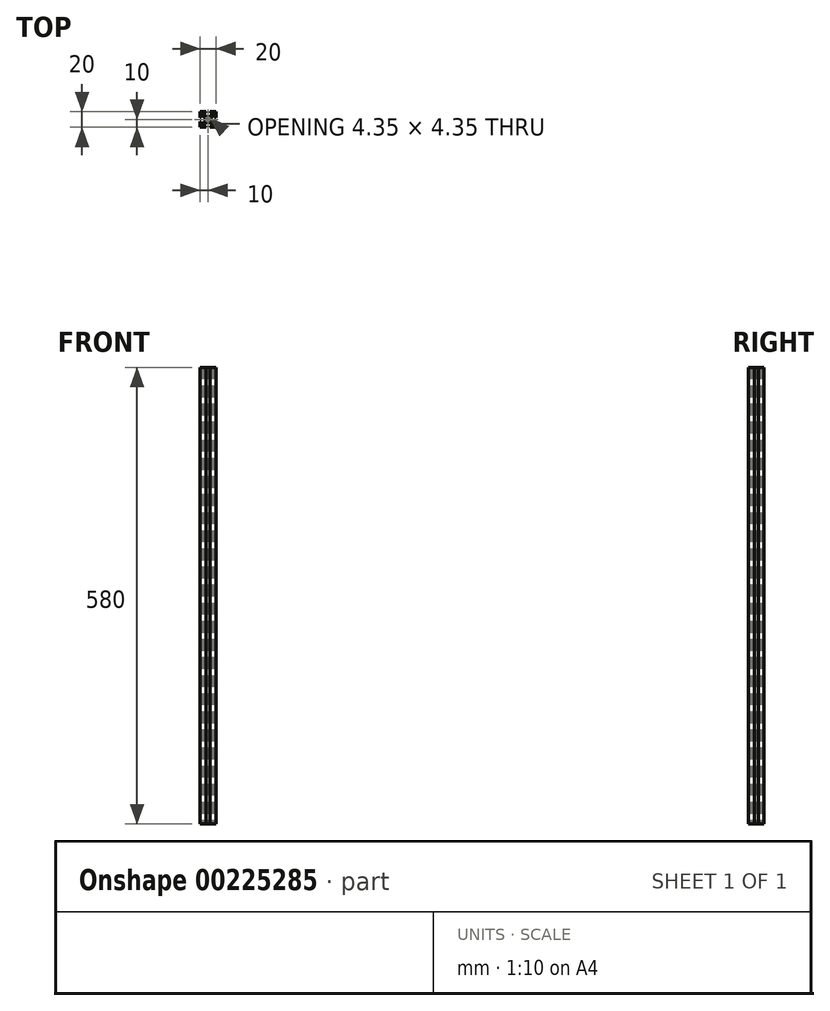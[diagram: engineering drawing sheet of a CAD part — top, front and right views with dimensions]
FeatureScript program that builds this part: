
annotation { "Feature Type Name" : "Feature", "Feature Type Description" : "" }
export const myFeature = defineFeature(function(context is Context, id is Id, definition is map)
    precondition{}
    {
        {
            var Q0;
            Q0=qCreatedBy(makeId("Top.planeOp"),FACE);
            var sketch = newSketch(context, id + "F0", { "sketchPlane" : qUnion([Q0])});
            skLineSegment(sketch, "E0.bottom", {"start": v(10, 10) * mm, "end": v(-10, 10) * mm});
            skLineSegment(sketch, "E0.top", {"start": v(10, -10) * mm, "end": v(-10, -10) * mm});
            skLineSegment(sketch, "E0.left", {"start": v(10, 10) * mm, "end": v(10, -10) * mm});
            skLineSegment(sketch, "E0.right", {"start": v(-10, 10) * mm, "end": v(-10, -10) * mm});
            skPoint(sketch, "E0.middle", {"position": v(0, 0) * mm});
            skLineSegment(sketch, "E1", {"start": v(-10, 10) * mm, "end": v(10, -10) * mm, "construction": true});
            skLineSegment(sketch, "E2", {"start": v(-10, -10) * mm, "end": v(10, 10) * mm, "construction": true});
            skLineSegment(sketch, "E3", {"start": v(0, 10) * mm, "end": v(0, -10) * mm, "construction": true});
            skLineSegment(sketch, "E4", {"start": v(-10, 0) * mm, "end": v(10, 0) * mm, "construction": true});
            skPoint(sketch, "E4.endSnap0", {"position": v(10, 0) * mm});
            skLineSegment(sketch, "E5", {"start": v(-2.63, 13.49) * mm, "end": v(2.63, 13.49) * mm});
            skLineSegment(sketch, "E6", {"start": v(2.63, 13.49) * mm, "end": v(2.63, 8.5) * mm});
            skLineSegment(sketch, "E7", {"start": v(2.63, 8.5) * mm, "end": v(6, 8.5) * mm});
            skLineSegment(sketch, "E8", {"start": v(6, 8.5) * mm, "end": v(6, 7.06) * mm});
            skLineSegment(sketch, "E9", {"start": v(6, 7.06) * mm, "end": v(2.6, 3.66) * mm});
            skLineSegment(sketch, "E10", {"start": v(2.6, 3.66) * mm, "end": v(-2.6, 3.66) * mm});
            skLineSegment(sketch, "E11", {"start": v(-2.6, 3.66) * mm, "end": v(-6, 7.06) * mm});
            skLineSegment(sketch, "E12", {"start": v(-6, 7.06) * mm, "end": v(-6, 8.5) * mm});
            skLineSegment(sketch, "E13", {"start": v(-6, 8.5) * mm, "end": v(-2.63, 8.5) * mm});
            skLineSegment(sketch, "E14", {"start": v(-2.63, 8.5) * mm, "end": v(-2.63, 13.49) * mm});
            skCircle(sketch, "E15", {"center": v(0, 0) * mm, "radius": 2.1 * mm});
            skLineSegment(sketch, "E16.MirrorCS", {"start": v(-7.06, 6) * mm, "end": v(-8.5, 6) * mm});
            skLineSegment(sketch, "E17.MirrorCS", {"start": v(-3.66, 2.6) * mm, "end": v(-7.06, 6) * mm});
            skLineSegment(sketch, "E18.MirrorCS", {"start": v(-8.5, 6) * mm, "end": v(-8.5, 2.63) * mm});
            skLineSegment(sketch, "E19.MirrorCS", {"start": v(-3.66, -2.6) * mm, "end": v(-3.66, 2.6) * mm});
            skLineSegment(sketch, "E20.MirrorCS", {"start": v(-7.06, -6) * mm, "end": v(-3.66, -2.6) * mm});
            skLineSegment(sketch, "E21.MirrorCS", {"start": v(-8.5, -6) * mm, "end": v(-7.06, -6) * mm});
            skLineSegment(sketch, "E22.MirrorCS", {"start": v(-8.5, -2.63) * mm, "end": v(-8.5, -6) * mm});
            skLineSegment(sketch, "E23.MirrorCS", {"start": v(-13.49, -2.63) * mm, "end": v(-8.5, -2.63) * mm});
            skLineSegment(sketch, "E24.MirrorCS", {"start": v(-13.49, 2.63) * mm, "end": v(-13.49, -2.63) * mm});
            skLineSegment(sketch, "E25.MirrorCS", {"start": v(-8.5, 2.63) * mm, "end": v(-13.49, 2.63) * mm});
            skLineSegment(sketch, "E26.MirrorCS", {"start": v(-2.6, -3.66) * mm, "end": v(-6, -7.06) * mm});
            skLineSegment(sketch, "E27.MirrorCS", {"start": v(2.6, -3.66) * mm, "end": v(-2.6, -3.66) * mm});
            skLineSegment(sketch, "E28.MirrorCS", {"start": v(6, -7.06) * mm, "end": v(2.6, -3.66) * mm});
            skLineSegment(sketch, "E29.MirrorCS", {"start": v(6, -8.5) * mm, "end": v(6, -7.06) * mm});
            skLineSegment(sketch, "E30.MirrorCS", {"start": v(2.63, -8.5) * mm, "end": v(6, -8.5) * mm});
            skLineSegment(sketch, "E31.MirrorCS", {"start": v(2.63, -13.49) * mm, "end": v(2.63, -8.5) * mm});
            skLineSegment(sketch, "E32.MirrorCS", {"start": v(-2.63, -13.49) * mm, "end": v(2.63, -13.49) * mm});
            skLineSegment(sketch, "E33.MirrorCS", {"start": v(-2.63, -8.5) * mm, "end": v(-2.63, -13.49) * mm});
            skLineSegment(sketch, "E34.MirrorCS", {"start": v(-6, -8.5) * mm, "end": v(-2.63, -8.5) * mm});
            skLineSegment(sketch, "E35.MirrorCS", {"start": v(-6, -7.06) * mm, "end": v(-6, -8.5) * mm});
            skLineSegment(sketch, "E36.MirrorCS", {"start": v(7.06, 6) * mm, "end": v(3.66, 2.6) * mm});
            skLineSegment(sketch, "E37.MirrorCS", {"start": v(8.5, 6) * mm, "end": v(7.06, 6) * mm});
            skLineSegment(sketch, "E38.MirrorCS", {"start": v(8.5, 2.63) * mm, "end": v(8.5, 6) * mm});
            skLineSegment(sketch, "E39.MirrorCS", {"start": v(13.49, 2.63) * mm, "end": v(8.5, 2.63) * mm});
            skLineSegment(sketch, "E40.MirrorCS", {"start": v(13.49, -2.63) * mm, "end": v(13.49, 2.63) * mm});
            skLineSegment(sketch, "E41.MirrorCS", {"start": v(8.5, -2.63) * mm, "end": v(13.49, -2.63) * mm});
            skLineSegment(sketch, "E42.MirrorCS", {"start": v(8.5, -6) * mm, "end": v(8.5, -2.63) * mm});
            skLineSegment(sketch, "E43.MirrorCS", {"start": v(7.06, -6) * mm, "end": v(8.5, -6) * mm});
            skLineSegment(sketch, "E44.MirrorCS", {"start": v(3.66, -2.6) * mm, "end": v(7.06, -6) * mm});
            skLineSegment(sketch, "E45.MirrorCS", {"start": v(3.66, 2.6) * mm, "end": v(3.66, -2.6) * mm});
            skCircle(sketch, "E46", {"center": v(-1.48, 1.48) * mm, "radius": 0.7 * mm});
            skCircle(sketch, "E47.MirrorC", {"center": v(1.48, 1.48) * mm, "radius": 0.7 * mm});
            skCircle(sketch, "E48.MirrorC", {"center": v(-1.48, -1.48) * mm, "radius": 0.7 * mm});
            skCircle(sketch, "E49.MirrorC", {"center": v(1.48, -1.48) * mm, "radius": 0.7 * mm});
            skSolve(sketch);
        }
        {
            var Q0;
            {var subQ29=sQuery(id+"F0.wireOp",EDGE,"E7");Q0=makeQuery(id+"F0.imprint","IMPRINT",FACE,{"disambiguationData":[TD([[makeQuery(id+"F0.imprint","IMPRINT",EDGE,{"derivedFrom":subQ29}),1.0]])]});}
            extrude(context, id + "F1", {"entities" : qUnion([Q0]), "depth" : 580 * mm});
        }
    });
